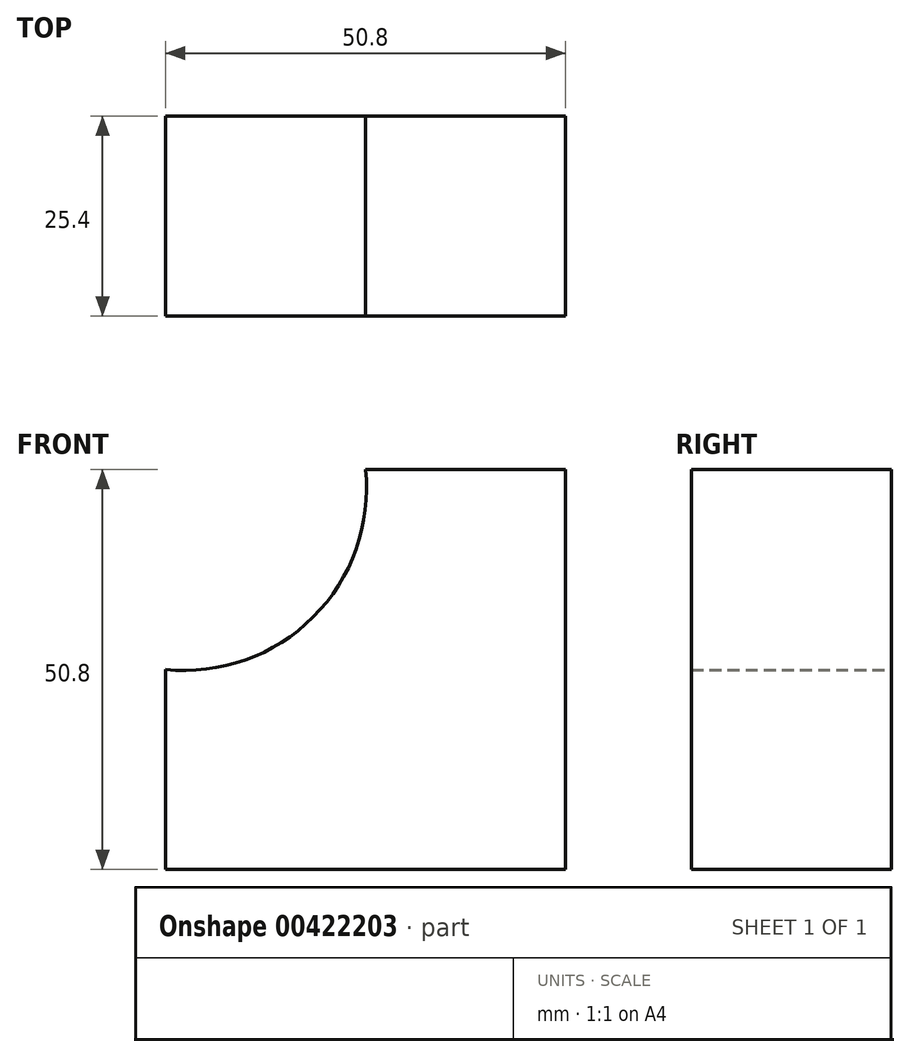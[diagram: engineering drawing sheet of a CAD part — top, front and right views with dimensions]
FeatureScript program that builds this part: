
annotation { "Feature Type Name" : "Feature", "Feature Type Description" : "" }
export const myFeature = defineFeature(function(context is Context, id is Id, definition is map)
    precondition{}
    {
        {
            var Q0;
            Q0=qCreatedBy(makeId("Front.planeOp"),FACE);
            var sketch = newSketch(context, id + "F0", { "sketchPlane" : qUnion([Q0])});
            skLineSegment(sketch, "E0", {"start": v(0, 0) * mm, "end": v(-50.8, 0) * mm});
            skLineSegment(sketch, "E1", {"start": v(0, 0) * mm, "end": v(0, 50.8) * mm});
            skLineSegment(sketch, "E2", {"start": v(0, 50.8) * mm, "end": v(-25.4, 50.8) * mm});
            skLineSegment(sketch, "E3", {"start": v(-50.8, 0) * mm, "end": v(-50.8, 25.4) * mm});
            skArc(sketch, "E4", {"start": v(-50.8, 25.4) * mm, "mid": v(-32.05, 32.05) * mm, "end": v(-25.4, 50.8) * mm});
            skSolve(sketch);
        }
        {
            var Q0;
            Q0 = qSketchRegion(id + "F0", true);
            extrude(context, id + "F1", {"entities" : qUnion([Q0]), "depth" : 25.4 * mm});
        }
    });
